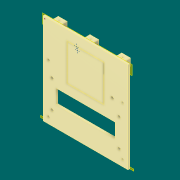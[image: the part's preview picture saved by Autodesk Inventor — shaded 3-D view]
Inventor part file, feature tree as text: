
AUTODESK INVENTOR PART (.ipt)
format: ipt  version: 2019 (Build 230136000, 136)  size: 349,696 bytes
history: native  units: mm
features: sketch x32, extrude x29, reference x17, other x6, plane x2
ambient origin geometry x8: Origin, YZ Plane, XZ Plane, XY Plane, X Axis, Y Axis, Z Axis, Center Point
bodies: Solid1 (feature_tree)
feature tree (86):
  plane  "Work Plane1"
  extrude  "Extrusion1"  Depth=8.0mm
  extrude  "Extrusion2"  Depth=8.0mm
  extrude  "Extrusion3"  Depth=5.0mm
  plane  "Work Plane2"
  extrude  "Extrusion4"  Depth=8.0mm TaperAngle=0.0deg
  extrude  "Extrusion5"  Depth=1.5mm
  extrude  "Extrusion6"  Depth=8.0mm TaperAngle=0.0deg
  extrude  "Extrusion7"  Depth=10.0mm
  extrude  "Extrusion8"  Depth=10.0mm
  extrude  "Extrusion9"  Depth=10.0mm
  extrude  "Extrusion10"  Depth=10.0mm
  extrude  "Extrusion11"  Depth=1.5mm
  extrude  "Extrusion12"  Depth=1.5mm
  extrude  "Extrusion13"  Depth=2.0mm TaperAngle=0.0deg
  extrude  "Extrusion14"  Depth=16.0mm
  sketch  "Sketch15"  dims[d43=66.0mm d44=2.0mm d45=0.0mm]
  extrude  "Extrusion15"  Depth=2.0mm TaperAngle=0.0deg
  extrude  "Extrusion16"  Depth=2.75mm
  extrude  "Extrusion17"  Depth=2.75mm
  extrude  "Extrusion18"  Depth=2.0mm TaperAngle=0.0deg
  extrude  "Extrusion19"  Depth=16.0mm
  extrude  "Extrusion20"  Depth=16.0mm
  extrude  "Extrusion21"  Depth=2.75mm
  sketch  "Sketch23"  dims[d89=2.75mm d92=2.75mm]
  extrude  "Extrusion22"  Depth=5.4mm
  extrude  "Extrusion23"  Depth=2.75mm
  extrude  "Extrusion24"  Depth=2.0mm TaperAngle=0.0deg
  sketch  "Sketch27"  dims[d118=3.0mm d119=2.0mm d120=0.0mm]
  extrude  "Extrusion25"  Depth=5.5mm
  extrude  "Extrusion26"  Depth=2.0mm TaperAngle=0.0deg
  extrude  "Extrusion27"  Depth=2.0mm TaperAngle=0.0deg
  extrude  "Extrusion28"  Depth=3.0mm
  extrude  "Extrusion29"  Depth=3.0mm
  sketch  "Sketch1"  dims[d0=10.0mm d1=8.0mm]
  reference  "Reference1"
  reference  "Reference2"
  reference  "Reference3"
  reference  "Reference4"
  reference  "Reference5"
  sketch  "Sketch2"  dims[d3=10.0mm d4=8.0mm]
  sketch  "Sketch3"  dims[d5=8.0mm d6=0.0mm d7=5.0mm]
  sketch  "Sketch4"  dims[d8=10.0mm d9=8.0mm d10=0.0mm]
  reference  "Reference6"
  reference  "Reference7"
  reference  "Reference8"
  sketch  "Sketch5"  dims[d12=1.5mm d14=1.5mm]
  sketch  "Sketch6"  dims[d16=1.5mm d17=8.0mm d18=0.0mm]
  reference  "Reference9"
  reference  "Reference10"
  reference  "Reference11"
  reference  "Reference12"
  reference  "Reference13"
  reference  "Reference14"
  sketch  "Sketch7"  dims[d19=10.0mm d20=10.0mm]
  sketch  "Sketch8"  dims[d21=10.0mm d22=10.0mm]
  sketch  "Sketch9"  dims[d24=5.0mm d25=10.0mm]
  sketch  "Sketch10"  dims[d26=10.0mm d27=10.0mm]
  sketch  "Sketch11"  dims[d28=8.0mm d29=0.0mm d31=1.5mm]
  sketch  "Sketch12"  dims[d33=1.5mm d35=1.5mm]
  sketch  "Sketch13"  dims[d36=10.0mm d37=0.0mm d38=2.0mm d39=0.0mm]
  sketch  "Sketch14"  dims[d41=33.0mm d42=16.0mm]
  sketch  "Sketch16"  dims[d50=2.75mm d54=2.75mm]
  sketch  "Sketch17"  dims[d61=2.75mm d64=2.75mm]
  sketch  "Sketch18"  dims[d65=2.0mm d66=0.0mm d67=2.0mm d68=0.0mm]
  sketch  "Sketch19"  dims[d70=33.0mm d71=16.0mm]
  sketch  "Sketch20"  dims[d72=66.0mm d73=16.0mm]
  sketch  "Sketch21"  dims[d74=33.0mm d80=2.75mm]
  sketch  "Sketch22"  dims[d83=2.75mm d84=5.4mm]
  sketch  "Sketch24"  dims[d93=2.0mm d94=0.0mm d96=2.0mm d97=0.0mm]
  reference  "Reference15"
  sketch  "Sketch25"  dims[d98=2.0mm d99=0.0mm d104=5.5mm]
  sketch  "Sketch26"  dims[d110=2.0mm d111=0.0mm d112=2.0mm d113=0.0mm]
  sketch  "Sketch28"  dims[d121=2.0mm d122=0.0mm d127=3.0mm]
  reference  "Reference16"
  sketch  "Sketch29"  dims[d128=2.0mm d129=0.0mm d134=3.0mm]
  reference  "Reference17"
  sketch  "Sketch30"  dims[d135=2.0mm d136=0.0mm]
  sketch  "Sketch31"  dims[d137=2.0mm d138=0.0mm]
  sketch  "Sketch32"  dims[d143=3.0mm d147=3.0mm d150=33.0mm d151=16.0mm d152=66.0mm d157=3.0mm d161=3.0mm d162=2.0mm d163=0.0mm d164=2.0mm d165=0.0mm d166=2.0mm d167=0.0mm d168=2.5mm d169=2.0mm d170=0.0mm d171=2.5mm d172=2.5mm d173=2.0mm d174=0.0mm d175=2.5mm d176=2.0mm d177=0.0mm d178=2.0mm d179=0.0mm d180=40.0mm d181=40.0mm d182=1.0mm d183=0.5mm d184=0.0mm d185=1.0mm d186=11.0mm d187=1.5mm d188=0.0mm d189=0.5mm d190=0.0mm]
  other  "Ensamblaje Reloj LCD 16x2.iam"
  other  "Down:1"
  other  "Lado izquierdo:1"
  other  "Lateral Derecho:1"
  other  "UP:1"
  other  "PCB Front:1"
